FCSTD DOCUMENT  (FreeCAD 1.0R39319 (Git))
Label: Assignment_9.1_Cooler_Assembly
License: All rights reserved
LicenseURL: https://en.wikipedia.org/wiki/All_rights_reserved
objects: App::Link×8, App::FeaturePython×8, Assembly::JointGroup×1, Assembly::AssemblyObject×1
EXTERNAL_REF file=Rectangular_part.FCStd obj=Extrude
EXTERNAL_REF file=Screw.FCStd obj=Screw
EXTERNAL_REF file=Nut.FCStd obj=Nut
EXTERNAL_REF file=Clamp.FCStd obj=Body

FEATURE [App::Link] Extrude
  LinkPlacement = pos=(35.2799,-3,38.4563) rot=(-0.691404,-0.510862,-0.510862;1.93173rad)
  LinkedObject = -> <external Rectangular_part.FCStd>#Extrude
  Placement = pos=(35.2799,-3,38.4563) rot=(-0.691404,-0.510862,-0.510862;1.93173rad)
FEATURE [App::Link] M5x20_Screw  label="M5x20-Screw"
  LinkPlacement = pos=(25,3,5) rot=(0,0.707107,0.707107;3.14159rad)
  LinkedObject = -> <external Screw.FCStd>#Screw
  Placement = pos=(25,3,5) rot=(0,0.707107,0.707107;3.14159rad)
FEATURE [App::Link] M5_Nut  label="M5-Nut"
  LinkPlacement = pos=(25,-6,5) rot=(0.585049,-0.573462,0.573462;2.08289rad)
  LinkedObject = -> <external Nut.FCStd>#Nut
  Placement = pos=(25,-6,5) rot=(0.585049,-0.573462,0.573462;2.08289rad)
FEATURE [App::Link] Extrude001
  LinkPlacement = pos=(-32.3502,-5e-15,39.2195) rot=(-0.496088,0.613961,-0.613961;4.06262rad)
  LinkedObject = -> <external Rectangular_part.FCStd>#Extrude
  Placement = pos=(-32.3502,-5e-15,39.2195) rot=(-0.496088,0.613961,-0.613961;4.06262rad)
FEATURE [App::Link] M5x20_Screw001  label="M5x20-Screw001"
  LinkPlacement = pos=(-25,3,5) rot=(0,0.707107,0.707107;3.14159rad)
  LinkedObject = -> <external Screw.FCStd>#Screw
  Placement = pos=(-25,3,5) rot=(0,0.707107,0.707107;3.14159rad)
FEATURE [App::Link] M5_Nut001  label="M5-Nut001"
  LinkPlacement = pos=(-25,-6,5) rot=(0,-0.707107,0.707107;3.14159rad)
  LinkedObject = -> <external Nut.FCStd>#Nut
  Placement = pos=(-25,-6,5) rot=(0,-0.707107,0.707107;3.14159rad)
FEATURE [App::Link] Body
  LinkedObject = -> <external Clamp.FCStd>#Body
FEATURE [App::FeaturePython] GroundedJoint  # Assembly grounded joint (typed FeaturePython)
  ObjectToGround = -> Body
FEATURE [App::Link] Body001
  LinkPlacement = pos=(0,-3,10) rot=(1,0,0;3.14159rad)
  LinkedObject = -> <external Clamp.FCStd>#Body
  Placement = pos=(0,-3,10) rot=(1,0,0;3.14159rad)
FEATURE [App::FeaturePython] Joint  label="Fixed"  # Assembly joint (typed FeaturePython)
  Activated = true
  AngleMax = 0
  AngleMin = 0
  Detach1 = false
  Detach2 = false
  Distance = 0
  Distance2 = 0
  EnableAngleMax = false
  EnableAngleMin = false
  EnableLengthMax = false
  EnableLengthMin = false
  JointType = 0 (Fixed)
  LengthMax = 0
  LengthMin = 0
  Placement2 = pos=(-25,3,5) rot=(0,0.707107,0.707107;3.14159rad)
  Reference1 = -> Assembly [M5x20_Screw001.Face17,M5x20_Screw001.Edge1]
  Reference2 = -> Assembly [Body.Edge33,Body.Edge33]
FEATURE [App::FeaturePython] Joint001  label="Fixed001"  # Assembly joint (typed FeaturePython)
  Activated = true
  AngleMax = 0
  AngleMin = 0
  Detach1 = false
  Detach2 = false
  Distance = 0
  Distance2 = 0
  EnableAngleMax = false
  EnableAngleMin = false
  EnableLengthMax = false
  EnableLengthMin = false
  JointType = 0 (Fixed)
  LengthMax = 0
  LengthMin = 0
  Placement2 = pos=(25,3,5) rot=(0,0.707107,0.707107;3.14159rad)
  Reference1 = -> Assembly [M5x20_Screw.Face17,M5x20_Screw.Edge1]
  Reference2 = -> Assembly [Body.Edge28,Body.Edge28]
FEATURE [App::FeaturePython] Joint002  label="Fixed002"  # Assembly joint (typed FeaturePython)
  Activated = true
  AngleMax = 0
  AngleMin = 0
  Detach1 = false
  Detach2 = false
  Distance = 0
  Distance2 = 0
  EnableAngleMax = false
  EnableAngleMin = false
  EnableLengthMax = false
  EnableLengthMin = false
  JointType = 0 (Fixed)
  LengthMax = 0
  LengthMin = 0
  Offset2 = pos=(0,0,-3) rot=(0,0,1;0rad)
  Placement1 = pos=(-25,2.2e-15,5) rot=(0,0.707107,0.707107;3.14159rad)
  Placement2 = pos=(-25,-3,5) rot=(0,0.707107,0.707107;3.14159rad)
  Reference1 = -> Assembly [Body001.Edge35,Body001.Edge35]
  Reference2 = -> Assembly [Body.Edge35,Body.Edge35]
FEATURE [App::FeaturePython] Joint003  label="Revolute"  # Assembly joint (typed FeaturePython)
  Activated = true
  AngleMax = 0
  AngleMin = 0
  Detach1 = false
  Detach2 = false
  Distance = 0
  Distance2 = 0
  EnableAngleMax = false
  EnableAngleMin = false
  EnableLengthMax = false
  EnableLengthMin = false
  JointType = 1 (Revolute)
  LengthMax = 0
  LengthMin = 0
  Placement1 = pos=(-35,-7.1e-15,-2e-15) rot=(0,0,1;0rad)
  Placement2 = pos=(-25,2.7e-15,5) rot=(0,0.707107,0.707107;3.14159rad)
  Reference1 = -> Assembly [Extrude001.Edge14,Extrude001.Edge14]
  Reference2 = -> Assembly [Body.Edge35,Body.Edge35]
FEATURE [App::FeaturePython] Joint004  label="Revolute001"  # Assembly joint (typed FeaturePython)
  Activated = true
  AngleMax = 0
  AngleMin = 0
  Detach1 = false
  Detach2 = false
  Distance = 0
  Distance2 = 0
  EnableAngleMax = false
  EnableAngleMin = false
  EnableLengthMax = false
  EnableLengthMin = false
  JointType = 1 (Revolute)
  LengthMax = 0
  LengthMin = 0
  Placement1 = pos=(-35,7.1e-15,3) rot=(0,0,1;0rad)
  Placement2 = pos=(25,9.8e-15,5) rot=(0,0.707107,0.707107;3.14159rad)
  Reference1 = -> Assembly [Extrude.Edge15,Extrude.Edge15]
  Reference2 = -> Assembly [Body.Edge11,Body.Edge11]
FEATURE [App::FeaturePython] Joint005  label="Revolute002"  # Assembly joint (typed FeaturePython)
  Activated = true
  AngleMax = 0
  AngleMin = 0
  Detach1 = false
  Detach2 = false
  Distance = 0
  Distance2 = 0
  EnableAngleMax = false
  EnableAngleMin = false
  EnableLengthMax = false
  EnableLengthMin = false
  JointType = 1 (Revolute)
  LengthMax = 0
  LengthMin = 0
  Placement2 = pos=(-25,3,5) rot=(0,0.707107,0.707107;3.14159rad)
  Reference1 = -> Assembly [M5_Nut001.Edge96,M5_Nut001.Edge96]
  Reference2 = -> Assembly [Body001.Edge33,Body001.Edge33]
FEATURE [App::FeaturePython] Joint006  label="Revolute003"  # Assembly joint (typed FeaturePython)
  Activated = true
  AngleMax = 0
  AngleMin = 0
  Detach1 = false
  Detach2 = false
  Distance = 0
  Distance2 = 0
  EnableAngleMax = false
  EnableAngleMin = false
  EnableLengthMax = false
  EnableLengthMin = false
  JointType = 1 (Revolute)
  LengthMax = 0
  LengthMin = 0
  Placement2 = pos=(25,3,5) rot=(0,0.707107,0.707107;3.14159rad)
  Reference1 = -> Assembly [M5_Nut.Edge96,M5_Nut.Edge96]
  Reference2 = -> Assembly [Body001.Edge28,Body001.Edge28]
FEATURE [Assembly::JointGroup] Joints
  Group = -> [GroundedJoint,Joint,Joint001,Joint002,Joint003,Joint004,Joint005,Joint006]
FEATURE [Assembly::AssemblyObject] Assembly
  Group = -> [Joints,Extrude,M5x20_Screw,M5_Nut,Extrude001,M5x20_Screw001,M5_Nut001,Body,GroundedJoint,Body001,Joint,Joint001,Joint002,Joint003,Joint004,Joint005,Joint006]
  Origin = -> Origin
  Type = Assembly

RESOLVED EXTERNAL PARTS (link-assembly join: the EXTERNAL_REF files above that resolve inside this repo's crawl, each included once):
---- part Clamp.FCStd = doc fcstd_bdafaa53ccf1 ----
FCSTD DOCUMENT  (FreeCAD 1.0R39319 (Git))
Label: Clamp
License: All rights reserved
LicenseURL: https://en.wikipedia.org/wiki/All_rights_reserved
objects: Sketcher::SketchObject×2, PartDesign::Pad×1, PartDesign::Pocket×1, PartDesign::Body×1
note: 11 computed .brp shape members not serialized (recipe doc carries the construction recipe); baked Part::Feature solids carry a one-line shape summary decoded from their .brp

FEATURE [Sketcher::SketchObject] Sketch
  ArcFitTolerance = 1e-06
  AttachmentSupport = -> [XY_Plane]
  FullyConstrained = true
  MakeInternals = false
  MapMode = 5
  sketch-geometry (11):
    g0: ArcOfCircle CenterX=-1.75e-14 CenterY=-9.4e-15 CenterZ=0 NormalX=0 NormalY=0 NormalZ=1 AngleXU=0 Radius=20.2237 StartAngle=0.14889 EndAngle=2.9927
    g1: LineSegment StartX=-17 StartY=2.7e-15 StartZ=0 EndX=-30 EndY=2.7e-15 EndZ=0
    g2: LineSegment StartX=-30 StartY=2.7e-15 StartZ=0 EndX=-30 EndY=3 EndZ=0
    g3: LineSegment StartX=-30 StartY=3 StartZ=0 EndX=-20 EndY=3 EndZ=0
    g4: LineSegment StartX=-17 StartY=3 StartZ=0 EndX=-17 EndY=2.7e-15 EndZ=0
    g5: LineSegment StartX=30 StartY=3 StartZ=0 EndX=20 EndY=3 EndZ=0
    g6: LineSegment StartX=20 StartY=3 StartZ=0 EndX=20 EndY=3 EndZ=0
    g7: LineSegment StartX=17 StartY=3 StartZ=0 EndX=17 EndY=9.8e-15 EndZ=0
    g8: LineSegment StartX=17 StartY=9.8e-15 StartZ=0 EndX=30 EndY=9.8e-15 EndZ=0
    g9: LineSegment StartX=30 StartY=9.8e-15 StartZ=0 EndX=30 EndY=3 EndZ=0
    g10: ArcOfCircle CenterX=-1.75e-14 CenterY=-9.4e-15 CenterZ=0 NormalX=0 NormalY=0 NormalZ=1 AngleXU=0 Radius=17.2627 StartAngle=0.174672 EndAngle=2.96692
  constraints (33):
    c: Coincident(g0,g-1)
    c: PointOnObject(g1,g-1)
    c: Horizontal(g1)
    c: Coincident(g2,g1)
    c: Vertical(g2)
    c: Horizontal(g3)
    c: Coincident(g3,g2)
    c: Vertical(g4)
    c: Coincident(g4,g1)
    c: Horizontal(g8)
    c: Coincident(g9,g8)
    c: Vertical(g9)
    c: Horizontal(g5)
    c: Coincident(g5,g9)
    c: Coincident(g6,g5)
    c: Horizontal(g6)
    c: Vertical(g7)
    c: Coincident(g7,g8)
    c: Equal(g3,g5)
    c: Equal(g9,g2)
    c: Equal(g1,g8)
    c: Coincident(g10,g0)
    c: Coincident(g0,g3)
    c: Coincident(g0,g6)
    c: Coincident(g7,g10)
    c: Coincident(g4,g10)
    c: PointOnObject(g8,g-1)
    c: Distance(g4,g0) = 3
    c: DistanceX(g5,g5) = 10
    c: DistanceY(g9,g9) = 3
    c: Distance(g9,g2) = 60
    c: DistanceY(g4,g4) = 3
    c: DistanceY(g7,g7) = 3
FEATURE [PartDesign::Pad] Pad
  Direction = (0,0,1)
  Length = 10
  Length2 = 10
  Profile = -> Sketch
  ReferenceAxis = -> Sketch [N_Axis]
  Refine = true
  Suppressed = false
  Type = 0
FEATURE [Sketcher::SketchObject] Sketch001
  ArcFitTolerance = 1e-06
  AttachmentSupport = -> [Pad]
  ExternalGeometry = -> [Pad]
  FullyConstrained = true
  MakeInternals = false
  MapMode = 5
  Placement = pos=(0,3,0) rot=(0,0.707107,0.707107;3.14159rad)
  sketch-geometry (2):
    g0: Circle CenterX=-25 CenterY=5 CenterZ=0 NormalX=0 NormalY=0 NormalZ=1 AngleXU=0 Radius=2.5
    g1: Circle CenterX=25 CenterY=5 CenterZ=0 NormalX=0 NormalY=0 NormalZ=1 AngleXU=0 Radius=2.5
  constraints (4):
    c: Symmetric(g-4,g-3,g0)
    c: Symmetric(g-5,g-6,g1)
    c: Diameter(g0) = 5
    c: Diameter(g1) = 5
FEATURE [PartDesign::Pocket] Pocket
  BaseFeature = -> Pad
  Direction = (0,-1,2e-16)
  Length = 5
  Length2 = 5
  Profile = -> Sketch001
  ReferenceAxis = -> Sketch001 [N_Axis]
  Refine = true
  Suppressed = false
  Type = 1
FEATURE [PartDesign::Body] Body
  AllowCompound = false
  Group = -> [Sketch,Pad,Sketch001,Pocket]
  Origin = -> Origin
  Tip = -> Pocket
---- part Rectangular_part.FCStd = doc fcstd_5674b394090c ----
FCSTD DOCUMENT  (FreeCAD 1.0R39319 (Git))
Label: Rectangular_part
License: All rights reserved
LicenseURL: https://en.wikipedia.org/wiki/All_rights_reserved
objects: Sketcher::SketchObject×1, Part::Extrusion×1
note: 3 computed .brp shape members not serialized (recipe doc carries the construction recipe); baked Part::Feature solids carry a one-line shape summary decoded from their .brp

FEATURE [Sketcher::SketchObject] Sketch
  ArcFitTolerance = 1e-06
  FullyConstrained = false
  MakeInternals = false
  sketch-geometry (16):
    g0: LineSegment StartX=-40 StartY=-6 StartZ=0 EndX=40 EndY=-6 EndZ=0
    g1: LineSegment StartX=40 StartY=-6 StartZ=0 EndX=40 EndY=6 EndZ=0
    g2: LineSegment StartX=40 StartY=6 StartZ=0 EndX=-40 EndY=6 EndZ=0
    g3: LineSegment StartX=-40 StartY=6 StartZ=0 EndX=-40 EndY=-6 EndZ=0
    g4: GeomPoint [constr] X=0 Y=0 Z=0
    g5: Circle CenterX=-35 CenterY=0 CenterZ=0 NormalX=0 NormalY=0 NormalZ=1 AngleXU=0 Radius=2.92349
    g6: LineSegment StartX=22.9457 StartY=-42.794 StartZ=0 EndX=22.9457 EndY=42.794 EndZ=0
    g7: LineSegment StartX=22.9457 StartY=42.794 StartZ=0 EndX=-22.9457 EndY=42.794 EndZ=0
    g8: LineSegment StartX=-22.9457 StartY=42.794 StartZ=0 EndX=-22.9457 EndY=-42.794 EndZ=0
    g9: LineSegment StartX=-22.9457 StartY=-42.794 StartZ=0 EndX=22.9457 EndY=-42.794 EndZ=0
    g10: GeomPoint [constr] X=0 Y=0 Z=0
    g11: LineSegment StartX=22.9457 StartY=-42.794 StartZ=0 EndX=22.9457 EndY=42.794 EndZ=0
    g12: LineSegment StartX=22.9457 StartY=42.794 StartZ=0 EndX=-22.9457 EndY=42.794 EndZ=0
    g13: LineSegment StartX=-22.9457 StartY=42.794 StartZ=0 EndX=-22.9457 EndY=-42.794 EndZ=0
    g14: LineSegment StartX=-22.9457 StartY=-42.794 StartZ=0 EndX=22.9457 EndY=-42.794 EndZ=0
    g15: GeomPoint [constr] X=0 Y=0 Z=0
  constraints (38):
    c: Coincident(g0,g1)
    c: Coincident(g1,g2)
    c: Coincident(g2,g3)
    c: Coincident(g3,g0)
    c: Horizontal(g0)
    c: Horizontal(g2)
    c: Vertical(g1)
    c: Vertical(g3)
    c: Symmetric(g2,g0,g4)
    c: Distance(g1,g3) = 80
    c: Distance(g0,g2) = 12
    c: Coincident(g4,g-1)
    c: PointOnObject(g5,g-1)
    c: Distance(g5,g3) = 5
    c: Coincident(g0,g1)
    c: Coincident(g1,g2)
    c: Coincident(g2,g3)
    c: Coincident(g3,g0)
    c: Vertical(g0)
    c: Vertical(g2)
    c: Horizontal(g1)
    c: Horizontal(g3)
    c: Symmetric(g2,g0,g4)
    c: Coincident(g4,g-1)
    c: Distance(g2,g2) = 85.588
    c: DistanceY(g2,g2) = 85.588
    c: Coincident(g0,g1)
    c: Coincident(g1,g2)
    c: Coincident(g2,g3)
    c: Coincident(g3,g0)
    c: Vertical(g0)
    c: Vertical(g2)
    c: Horizontal(g1)
    c: Horizontal(g3)
    c: Symmetric(g2,g0,g4)
    c: Coincident(g4,g-1)
    c: Distance(g2,g2) = 85.588
    c: DistanceY(g2,g2) = 85.588
FEATURE [Part::Extrusion] Extrude
  Base = -> Sketch
  Dir = (0,0,1)
  DirMode = 2
  FaceMakerClass = Part::FaceMakerBullseye
  FaceMakerMode = 3
  LengthFwd = 3
  LengthRev = 0
  Solid = true
  Symmetric = false
